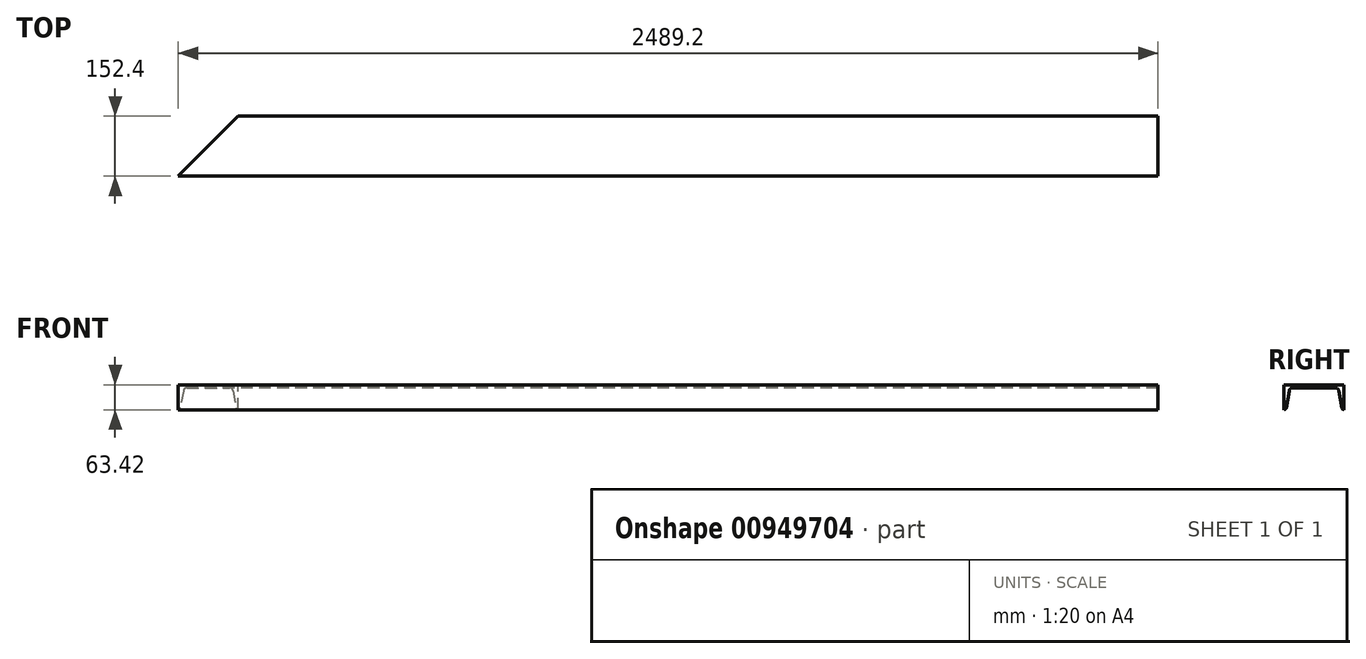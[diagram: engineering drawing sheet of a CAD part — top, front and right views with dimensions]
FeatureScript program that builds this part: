
annotation { "Feature Type Name" : "Feature", "Feature Type Description" : "" }
export const myFeature = defineFeature(function(context is Context, id is Id, definition is map)
    precondition{}
    {
        {
            var Q0;
            Q0=qCreatedBy(makeId("Right.planeOp"),FACE);
            var sketch = newSketch(context, id + "F0", { "sketchPlane" : qUnion([Q0])});
            skLineSegment(sketch, "E0", {"start": v(-76.2, 0) * mm, "end": v(76.2, 0) * mm});
            skLineSegment(sketch, "E1", {"start": v(76.2, 0) * mm, "end": v(76.2, -63.42) * mm});
            skLineSegment(sketch, "E2", {"start": v(-76.2, 0) * mm, "end": v(-76.2, -63.42) * mm});
            skLineSegment(sketch, "E3", {"start": v(-63.12, -15.57) * mm, "end": v(-70.65, -58.76) * mm});
            skLineSegment(sketch, "E4", {"start": v(63.12, -15.57) * mm, "end": v(70.65, -58.76) * mm});
            skLineSegment(sketch, "E5", {"start": v(-53.98, -7.87) * mm, "end": v(53.98, -7.87) * mm});
            skArc(sketch, "E6.filletArc", {"start": v(-76.2, -63.42) * mm, "mid": v(-72.57, -62.1) * mm, "end": v(-70.65, -58.76) * mm});
            skArc(sketch, "E7.filletArc", {"start": v(70.65, -58.76) * mm, "mid": v(72.57, -62.1) * mm, "end": v(76.2, -63.42) * mm});
            skArc(sketch, "E8.filletArc", {"start": v(-53.98, -7.87) * mm, "mid": v(-59.95, -10.05) * mm, "end": v(-63.12, -15.57) * mm});
            skArc(sketch, "E9.filletArc", {"start": v(63.12, -15.57) * mm, "mid": v(59.95, -10.05) * mm, "end": v(53.98, -7.87) * mm});
            skSolve(sketch);
        }
        {
            var Q0;
            Q0=qSketchRegion(id+"F0",true);
            extrude(context, id + "F1", {"entities" : qUnion([Q0]), "depth" : 2489.2 * mm, "offsetDistance" : 25.4 * mm});
        }
        {
            var Q0;
            Q0=makeQuery(id+"F1.opExtrude","SWEPT_FACE",FACE,{"disambiguationData":[OSD([sQuery(id+"F0.wireOp",EDGE,"E0")])]});
            var sketch = newSketch(context, id + "F2", { "sketchPlane" : qUnion([Q0])});
            skLineSegment(sketch, "E10", {"start": v(0, -76.2) * mm, "end": v(152.4, 76.2) * mm});
            skLineSegment(sketch, "E11", {"start": v(152.4, 76.2) * mm, "end": v(0, 76.2) * mm});
            skLineSegment(sketch, "E12", {"start": v(0, 76.2) * mm, "end": v(0, -76.2) * mm});
            skSolve(sketch);
        }
        {
            var Q0;
            Q0=qSketchRegion(id+"F2",true);
            extrude(context, id + "F3", {"entities" : qUnion([Q0]), "operationType" : NewBodyOperationType.REMOVE, "endBound" : BoundingType.THROUGH_ALL, "oppositeDirection" : true, "depth" : 25.4 * mm, "offsetDistance" : 25.4 * mm});
        }
    });
